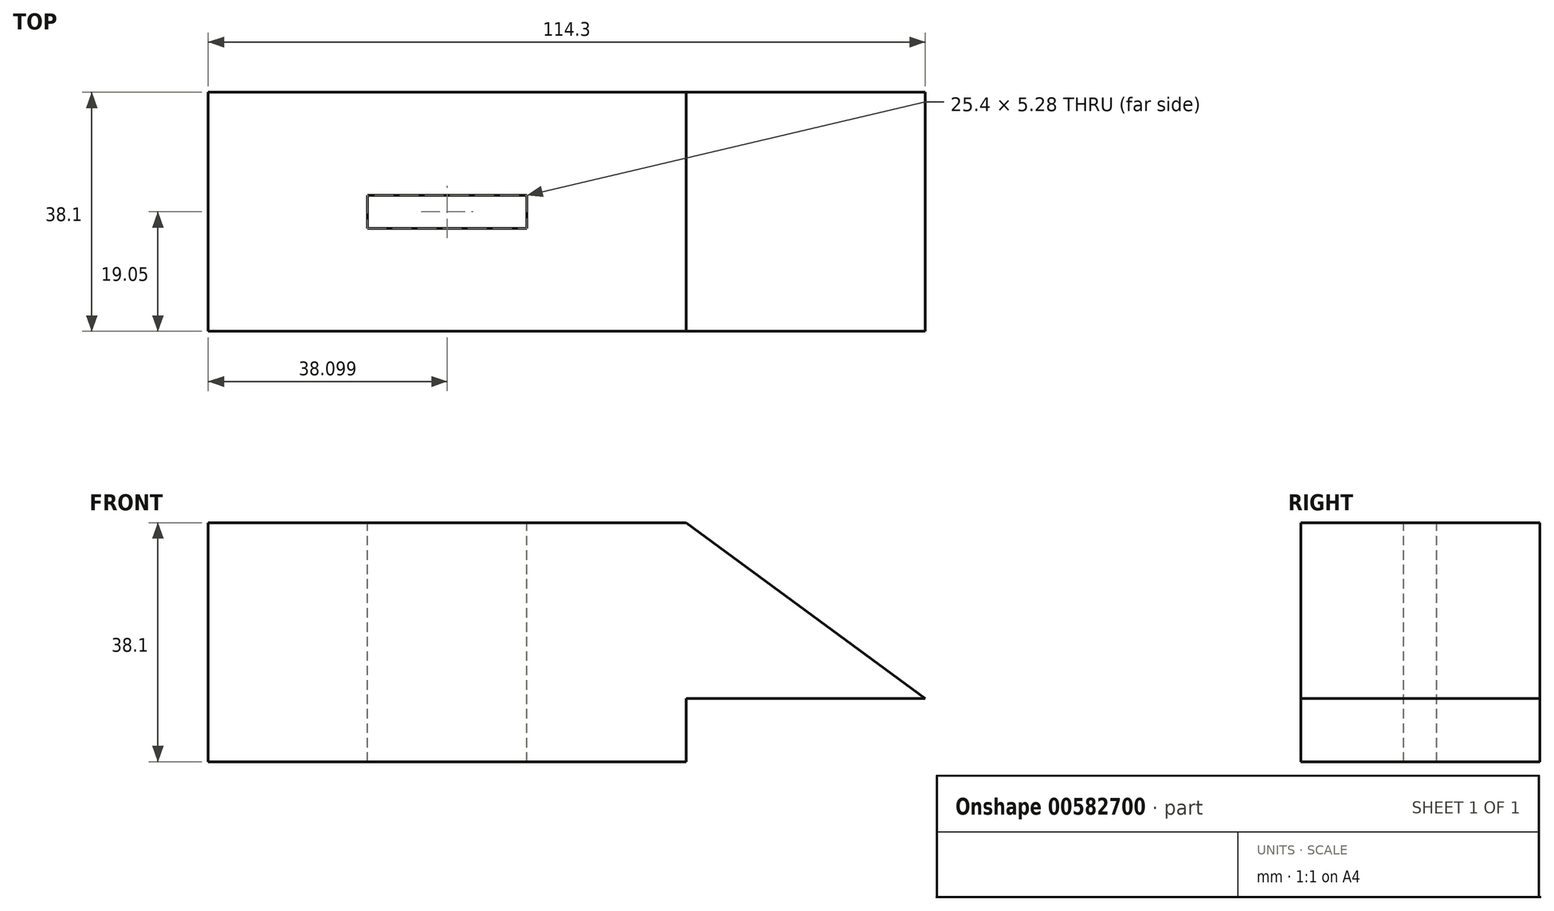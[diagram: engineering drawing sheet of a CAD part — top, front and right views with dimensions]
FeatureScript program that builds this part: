
annotation { "Feature Type Name" : "Feature", "Feature Type Description" : "" }
export const myFeature = defineFeature(function(context is Context, id is Id, definition is map)
    precondition{}
    {
        {
            var Q0;
            Q0=qCreatedBy(makeId("Front.planeOp"),FACE);
            var sketch = newSketch(context, id + "F0", { "sketchPlane" : qUnion([Q0])});
            skLineSegment(sketch, "E0", {"start": v(11.27, 8.47) * mm, "end": v(11.27, 18.55) * mm});
            skLineSegment(sketch, "E1", {"start": v(11.27, 18.55) * mm, "end": v(49.37, 18.55) * mm});
            skLineSegment(sketch, "E2", {"start": v(49.37, 18.55) * mm, "end": v(11.27, 46.57) * mm});
            skLineSegment(sketch, "E3", {"start": v(-64.93, 46.57) * mm, "end": v(11.27, 46.57) * mm});
            skLineSegment(sketch, "E4", {"start": v(-64.93, 8.47) * mm, "end": v(11.27, 8.47) * mm});
            skLineSegment(sketch, "E5", {"start": v(-64.93, 8.47) * mm, "end": v(-64.93, 46.57) * mm});
            skSolve(sketch);
        }
        {
            var Q0;
            Q0 = qSketchRegion(id + "F0", true);
            extrude(context, id + "F1", {"entities" : qUnion([Q0]), "depth" : 38.1 * mm, "offsetDistance" : 25.4 * mm});
        }
        {
            var Q0;
            Q0=makeQuery(id+"F1.opExtrude","SWEPT_FACE",FACE,{"disambiguationData":[OSD([sQuery(id+"F0.wireOp",EDGE,"E3")])]});
            var sketch = newSketch(context, id + "F2", { "sketchPlane" : qUnion([Q0])});
            skLineSegment(sketch, "E6", {"start": v(-26.83, -21.7) * mm, "end": v(-14.13, -21.7) * mm});
            skLineSegment(sketch, "E7", {"start": v(-14.13, -21.7) * mm, "end": v(-14.13, -16.4) * mm});
            skLineSegment(sketch, "E8", {"start": v(-26.83, -21.7) * mm, "end": v(-39.53, -21.7) * mm});
            skPoint(sketch, "E9", {"position": v(-14.13, -19.05) * mm});
            skLineSegment(sketch, "E10", {"start": v(-14.13, -16.4) * mm, "end": v(-39.53, -16.4) * mm});
            skLineSegment(sketch, "E11", {"start": v(-39.53, -16.4) * mm, "end": v(-39.53, -21.7) * mm});
            skSolve(sketch);
        }
        {
            var Q0;
            Q0 = qSketchRegion(id + "F2", true);
            extrude(context, id + "F3", {"entities" : qUnion([Q0]), "operationType" : NewBodyOperationType.REMOVE, "oppositeDirection" : true, "depth" : 38.1 * mm, "offsetDistance" : 25.4 * mm});
        }
    });
